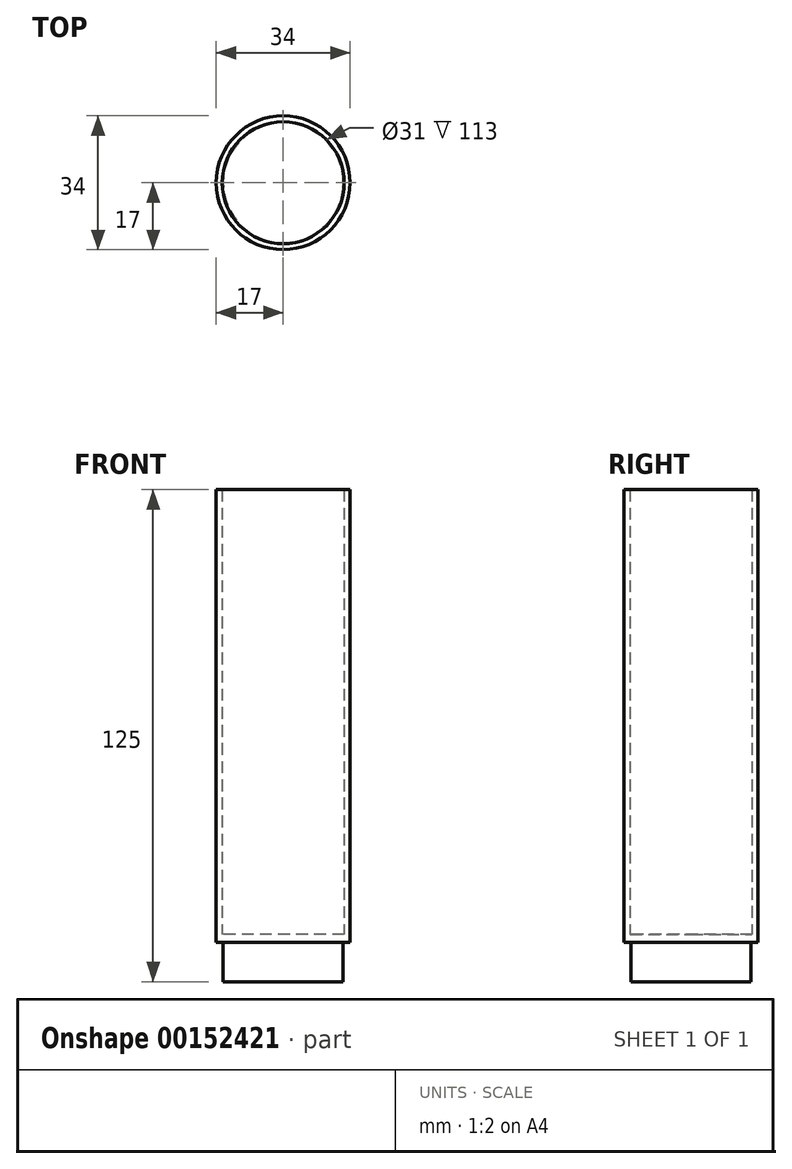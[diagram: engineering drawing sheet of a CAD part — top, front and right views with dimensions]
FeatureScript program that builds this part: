
annotation { "Feature Type Name" : "Feature", "Feature Type Description" : "" }
export const myFeature = defineFeature(function(context is Context, id is Id, definition is map)
    precondition{}
    {
        {
            var Q0;
            Q0=qCreatedBy(makeId("Top.planeOp"),FACE);
            cPlane(context, id + "F0", {"entities" : qUnion([Q0]), "cplaneType" : CPlaneType.OFFSET, "offset" : (222) * mm, "width" : 150 * mm, "height" : 150 * mm});
        }
        {
            var Q0;
            Q0=qCreatedBy(id+"F0.planeOp",FACE);
            var sketch = newSketch(context, id + "F1", { "sketchPlane" : qUnion([Q0])});
            skCircle(sketch, "E0", {"center": v(0, 0) * mm, "radius": 17 * mm});
            skCircle(sketch, "E1", {"center": v(0, 0) * mm, "radius": 15.5 * mm});
            skSolve(sketch);
        }
        {
            var Q0;
            Q0=qSketchRegion(id+"F1",true);
            extrude(context, id + "F2", {"entities" : qUnion([Q0]), "depth" : 115 * mm});
        }
        {
            var Q0;
            Q0=qCreatedBy(id+"F0.planeOp",FACE);
            var sketch = newSketch(context, id + "F3", { "sketchPlane" : qUnion([Q0])});
            skCircle(sketch, "E2.0", {"center": v(0, 0) * mm, "radius": 17 * mm});
            skSolve(sketch);
        }
        {
            var Q0;
            Q0=makeQuery(id+"F3.imprint","IMPRINT",FACE,{"disambiguationData":[TD([[makeQuery(id+"F3.imprint","IMPRINT",EDGE,{"derivedFrom":sQuery(id+"F3.wireOp",EDGE,"E2.0")}),1.0]])]});
            extrude(context, id + "F4", {"entities" : qUnion([Q0]), "operationType" : NewBodyOperationType.ADD, "depth" : 2 * mm});
        }
        {
            var Q0;
            Q0=makeQuery(id+"F4.boolean.opBoolean","MERGE",FACE,{"derivedFrom":[makeQuery(id+"F2.opExtrude","CAP_FACE",FACE,{"disambiguationData":[OSD([sQuery(id+"F1.wireOp",EDGE,"E0"),sQuery(id+"F1.wireOp",EDGE,"E1")])],"isStart":true}),makeQuery(id+"F4.opExtrude","CAP_FACE",FACE,{"disambiguationData":[OSD([sQuery(id+"F3.wireOp",EDGE,"E2.0")])],"isStart":true})]});
            var sketch = newSketch(context, id + "F5", { "sketchPlane" : qUnion([Q0])});
            skCircle(sketch, "E3", {"center": v(0, 0) * mm, "radius": 15.25 * mm});
            skSolve(sketch);
        }
        {
            var Q0;
            Q0=qSketchRegion(id+"F5",true);
            extrude(context, id + "F6", {"entities" : qUnion([Q0]), "operationType" : NewBodyOperationType.ADD, "depth" : 10 * mm});
        }
    });
